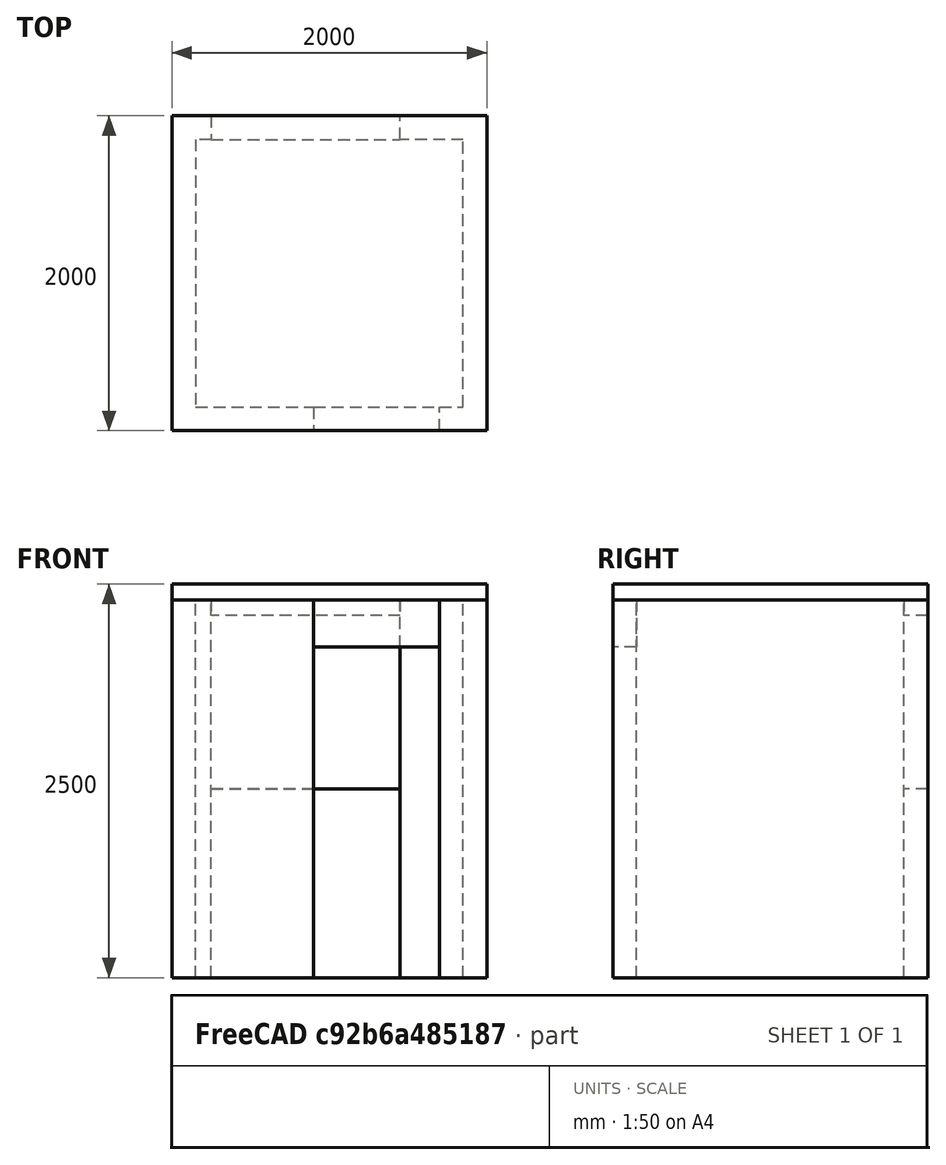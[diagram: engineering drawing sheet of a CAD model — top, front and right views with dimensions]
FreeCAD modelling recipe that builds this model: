
FCSTD DOCUMENT  (FreeCAD 0.16R6123 +2 (Git))
Label: cabin
License: CreativeCommons Attribution
LicenseURL: http://creativecommons.org/licenses/by/4.0/
objects: Part::Part2DObjectPython×22, App::FeaturePython×13, App::DocumentObjectGroup×6, Part::Extrusion×6, App::Annotation×3, Part::Feature×2
note: 30 computed .brp shape members not serialized (recipe doc carries the construction recipe); baked Part::Feature solids carry a one-line shape summary decoded from their .brp

FEATURE [Part::Part2DObjectPython] Rectangle  # Draft 2D object (typed FeaturePython)
  ChamferSize = 0
  Columns = 1
  FilletRadius = 0
  Height = 2000
  Length = 2000
  MakeFace = true
  Rows = 1
FEATURE [Part::Part2DObjectPython] Rectangle001  # Draft 2D object (typed FeaturePython)
  ChamferSize = 0
  Columns = 1
  FilletRadius = 0
  Height = 1700
  Length = 1700
  MakeFace = true
  Placement = pos=(150,150,0) rot=(0,0,1;0rad)
  Rows = 1
FEATURE [Part::Part2DObjectPython] Line  # Draft 2D object (typed FeaturePython)
  ChamferSize = 0
  Closed = false
  End = (1850,-930.924,0)
  FilletRadius = 0
  Length = 1930.92
  MakeFace = true
  Points = (2) [(1850,1000,0),(1850,-930.924,0)]
  Start = (1850,1000,0)
  Subdivisions = 0
FEATURE [Part::Part2DObjectPython] Line001  # Draft 2D object (typed FeaturePython)
  ChamferSize = 0
  Closed = false
  End = (1700,-930.924,0)
  FilletRadius = 0
  Length = 1930.92
  MakeFace = true
  Placement = pos=(-150,0,0) rot=(0,0,1;0rad)
  Points = (2) [(1850,1000,0),(1850,-930.924,0)]
  Start = (1700,1000,0)
  Subdivisions = 0
FEATURE [Part::Part2DObjectPython] Line002  # Draft 2D object (typed FeaturePython)
  ChamferSize = 0
  Closed = false
  End = (900,-930.924,0)
  FilletRadius = 0
  Length = 1930.92
  MakeFace = true
  Placement = pos=(-950,0,0) rot=(0,0,1;0rad)
  Points = (2) [(1850,1000,0),(1850,-930.924,0)]
  Start = (900,1000,0)
  Subdivisions = 0
FEATURE [Part::Part2DObjectPython] Line003  # Draft 2D object (typed FeaturePython)
  ChamferSize = 0
  Closed = false
  End = (150,2719.11,0)
  FilletRadius = 0
  Length = 1719.11
  MakeFace = true
  Points = (2) [(150,1000,0),(150,2719.11,0)]
  Start = (150,1000,0)
  Subdivisions = 0
FEATURE [Part::Part2DObjectPython] Line004  # Draft 2D object (typed FeaturePython)
  ChamferSize = 0
  Closed = false
  End = (250,2719.11,0)
  FilletRadius = 0
  Length = 1719.11
  MakeFace = true
  Placement = pos=(100,0,0) rot=(0,0,1;0rad)
  Points = (2) [(150,1000,0),(150,2719.11,0)]
  Start = (250,1000,0)
  Subdivisions = 0
FEATURE [Part::Part2DObjectPython] Line005  # Draft 2D object (typed FeaturePython)
  ChamferSize = 0
  Closed = false
  End = (1450,2719.11,0)
  FilletRadius = 0
  Length = 1719.11
  MakeFace = true
  Placement = pos=(1300,0,0) rot=(0,0,1;0rad)
  Points = (2) [(150,1000,0),(150,2719.11,0)]
  Start = (1450,1000,0)
  Subdivisions = 0
FEATURE [App::DocumentObjectGroup] Construction
  Group = -> [Rectangle,Rectangle001,Line,Line001,Line002,Line003,Line004,Line005]
FEATURE [Part::Part2DObjectPython] DWire  # Draft 2D object (typed FeaturePython)
  ChamferSize = 0
  Closed = true
  End = (0,0,0)
  FilletRadius = 0
  Length = 6000
  MakeFace = true
  Points = (8) [(0,2000,0),(250,2000,0),(250,1850,0),(150,1850,0),(150,150,0),(900,150,0),(900,0,0),(0,0,0)]
  Start = (0,2000,0)
  Subdivisions = 0
FEATURE [Part::Part2DObjectPython] DWire001  # Draft 2D object (typed FeaturePython)
  ChamferSize = 0
  Closed = true
  End = (1850,1850,0)
  FilletRadius = 0
  Length = 5400
  MakeFace = true
  Points = (8) [(1450,1850,0),(1450,2000,0),(2000,2000,0),(2000,0,0),(1700,0,0),(1700,150,0),(1850,150,0),(1850,1850,0)]
  Start = (1450,1850,0)
  Subdivisions = 0
FEATURE [Part::Part2DObjectPython] Line006  # Draft 2D object (typed FeaturePython)
  ChamferSize = 0
  Closed = false
  End = (1450,1925,0)
  FilletRadius = 0
  Length = 1200
  MakeFace = true
  Points = (2) [(250,1925,0),(1450,1925,0)]
  Start = (250,1925,0)
  Subdivisions = 0
FEATURE [Part::Part2DObjectPython] Line007  # Draft 2D object (typed FeaturePython)
  ChamferSize = 0
  Closed = false
  End = (1700,75,0)
  FilletRadius = 0
  Length = 800
  MakeFace = true
  Placement = pos=(1625,1775,0) rot=(0,0,-1;1.5708rad)
  Points = (2) [(900,75,0),(1700,75,0)]
  Start = (1700,875,0)
  Subdivisions = 0
FEATURE [Part::Part2DObjectPython] Arc  # Draft 2D object (typed FeaturePython)
  FirstAngle = 90
  LastAngle = 180
  MakeFace = true
  Placement = pos=(1700,75,0) rot=(0,0,1;0rad)
  Radius = 800
FEATURE [Part::Part2DObjectPython] Rectangle002  label="Tabletop"  # Draft 2D object (typed FeaturePython)
  ChamferSize = 0
  Columns = 1
  FilletRadius = 0
  Height = -600
  Length = 1700
  MakeFace = true
  Placement = pos=(150,1850,0) rot=(0,0,1;0rad)
  Rows = 1
FEATURE [Part::Feature] ENTITIES_  label="sink"
  Placement = pos=(-18300.5,-3837.71,0) rot=(0,0,1;0rad)
  shape: bbox 850 x 500 x 2e-07 mm, 0 faces, 0 solids (baked)
FEATURE [Part::Feature] ENTITIES_0  label="cooktop"
  Placement = pos=(-6228.71,-15812.2,-2.2e-11) rot=(0,0,1;0rad)
  shape: bbox 500 x 600 x 2e-07 mm, 0 faces, 0 solids (baked)
FEATURE [Part::Part2DObjectPython] Rectangle003  # Draft 2D object (typed FeaturePython)
  ChamferSize = 0
  Columns = 1
  FilletRadius = 0
  Height = -150
  Length = 1200
  MakeFace = true
  Placement = pos=(250,2000,0) rot=(0,0,1;0rad)
  Rows = 1
FEATURE [Part::Part2DObjectPython] Rectangle004  # Draft 2D object (typed FeaturePython)
  ChamferSize = 0
  Columns = 1
  FilletRadius = 0
  Height = 150
  Length = -800
  MakeFace = true
  Placement = pos=(1700,0,0) rot=(0,0,1;0rad)
  Rows = 1
FEATURE [App::FeaturePython] Dimension  # Draft dimension (typed FeaturePython)
  Dimline = (491.097,338.831,0)
  Direction = (0,0,0)
  Distance = 150
  End = (0,150,0)
  Normal = (0,0,1)
  Start = (0,0,0)
FEATURE [App::FeaturePython] Dimension003  # Draft dimension (typed FeaturePython)
  Dimline = (491.097,1850,0)
  Direction = (0,0,0)
  Distance = 150
  End = (250,2000,0)
  Normal = (0,0,1)
  Start = (250,1850,0)
FEATURE [App::FeaturePython] Dimension004  # Draft dimension (typed FeaturePython)
  Dimline = (491.097,1850,0)
  Direction = (0,0,0)
  Distance = 1700
  End = (150,1850,0)
  Normal = (0,0,1)
  Start = (150,150,0)
FEATURE [App::FeaturePython] Dimension005  # Draft dimension (typed FeaturePython)
  Dimline = (-280.313,430.313,0)
  Direction = (0,0,0)
  Distance = 150
  End = (150,0,0)
  Normal = (0,0,1)
  Start = (0,0,0)
FEATURE [App::FeaturePython] Dimension006  # Draft dimension (typed FeaturePython)
  Dimline = (0,430.313,0)
  Direction = (0,0,0)
  Distance = 1700
  End = (1850,150,0)
  Normal = (0,0,1)
  Start = (150,150,0)
FEATURE [App::FeaturePython] Dimension007  # Draft dimension (typed FeaturePython)
  Dimline = (1850,430.313,0)
  Direction = (0,0,0)
  Distance = 150
  End = (2000,150,0)
  Normal = (0,0,1)
  Start = (1850,150,0)
FEATURE [App::FeaturePython] Dimension008  # Draft dimension (typed FeaturePython)
  Dimline = (159.788,2397.37,0)
  Direction = (0,0,0)
  Distance = 250
  End = (250,2000,0)
  Normal = (0,0,1)
  Start = (0,2000,0)
FEATURE [App::FeaturePython] Dimension009  # Draft dimension (typed FeaturePython)
  Dimline = (171.744,2397.37,0)
  Direction = (0,0,0)
  Distance = 1200
  End = (1450,2000,0)
  Normal = (0,0,1)
  Start = (250,2000,0)
FEATURE [App::FeaturePython] Dimension010  # Draft dimension (typed FeaturePython)
  Dimline = (1268.19,2397.37,0)
  Direction = (0,0,0)
  Distance = 550
  End = (2000,2000,0)
  Normal = (0,0,1)
  Start = (1450,2000,0)
FEATURE [App::FeaturePython] Dimension011  # Draft dimension (typed FeaturePython)
  Dimline = (-372.676,1627.32,0)
  Direction = (0,0,0)
  Distance = 2000
  End = (0,2000,0)
  Normal = (0,0,1)
  Start = (0,0,0)
FEATURE [App::FeaturePython] Dimension012  # Draft dimension (typed FeaturePython)
  Dimline = (900,-572.516,0)
  Direction = (0,0,0)
  Distance = 900
  End = (900,0,0)
  Normal = (0,0,1)
  Start = (0,0,0)
FEATURE [App::FeaturePython] Dimension013  # Draft dimension (typed FeaturePython)
  Dimline = (900,-572.516,0)
  Direction = (0,0,0)
  Distance = 800
  End = (1700,0,0)
  Normal = (0,0,1)
  Start = (900,0,0)
FEATURE [App::FeaturePython] Dimension014  # Draft dimension (typed FeaturePython)
  Dimline = (1700,-572.516,0)
  Direction = (0,0,0)
  Distance = 300
  End = (2000,0,0)
  Normal = (0,0,1)
  Start = (1700,0,0)
FEATURE [Part::Part2DObjectPython] DWire002  # Draft 2D object (typed FeaturePython)
  ChamferSize = 0
  Closed = false
  End = (1363.02,83.2838,0)
  FilletRadius = 0
  Length = 1405.75
  MakeFace = true
  Points = (3) [(2622.62,-269.561,0),(1715.86,-269.561,0),(1363.02,83.2838,0)]
  Start = (2622.62,-269.561,0)
  Subdivisions = 0
FEATURE [App::Annotation] Text
  LabelText = wooden door
  Position = (2665.06,-304.996,0)
FEATURE [Part::Part2DObjectPython] Line008  # Draft 2D object (typed FeaturePython)
  ChamferSize = 0
  Closed = false
  End = (1776,1520.9,0)
  FilletRadius = 0
  Length = 906.803
  MakeFace = true
  Points = (2) [(2682.8,1520.9,0),(1776,1520.9,0)]
  Start = (2682.8,1520.9,0)
  Subdivisions = 0
FEATURE [App::Annotation] Text001
  LabelText = wooden tabletop | height = 1.10m
  Position = (2760.04,1562.41,0)
FEATURE [Part::Part2DObjectPython] DWire003  # Draft 2D object (typed FeaturePython)
  ChamferSize = 0
  Closed = false
  End = (967.987,1949.52,0)
  FilletRadius = 0
  Length = 1831.67
  MakeFace = true
  Points = (3) [(2696.08,2244.4,0),(1335.95,2244.4,0),(967.987,1949.52,0)]
  Start = (2696.08,2244.4,0)
  Subdivisions = 0
FEATURE [App::Annotation] Text002
  LabelText = aluminium window frame | with single-thickness glass
  Position = (2764.09,2281.21,0)
FEATURE [App::DocumentObjectGroup] Group  label="Annotations"
  Group = -> [Dimension,Dimension003,Dimension004,Dimension005,Dimension006,Dimension007,Dimension008,Dimension009,Dimension010,Dimension011,Dimension012,Dimension013,Dimension014,DWire002,Text,Line008,Text001,DWire003,Text002]
FEATURE [App::DocumentObjectGroup] Group001  label="Furniture"
  Group = -> [ENTITIES_0,ENTITIES_,Rectangle002]
FEATURE [App::DocumentObjectGroup] Group002  label="Doors & Windows"
  Group = -> [Line006,Rectangle003,Arc,Line007,Rectangle004]
FEATURE [Part::Extrusion] Extrusion
  Base = -> DWire
  Dir = (0,0,2400)
  Solid = true
FEATURE [Part::Extrusion] Extrusion001
  Base = -> DWire001
  Dir = (0,0,2400)
  Solid = true
FEATURE [Part::Part2DObjectPython] Rectangle005  # Draft 2D object (typed FeaturePython)
  ChamferSize = 0
  Columns = 1
  FilletRadius = 0
  Height = -150
  Length = 800
  MakeFace = true
  Placement = pos=(900,150,2400) rot=(0,0,1;0rad)
  Rows = 1
  Support = -> Extrusion
FEATURE [Part::Extrusion] Extrusion002
  Base = -> Rectangle005
  Dir = (0,0,-300)
  Solid = true
FEATURE [Part::Part2DObjectPython] Rectangle006  # Draft 2D object (typed FeaturePython)
  ChamferSize = 0
  Columns = 1
  FilletRadius = 0
  Height = -150
  Length = -1200
  MakeFace = true
  Placement = pos=(1450,2000,2400) rot=(0,0,1;0rad)
  Rows = 1
FEATURE [Part::Extrusion] Extrusion003
  Base = -> Rectangle003
  Dir = (0,0,1200)
  Solid = true
FEATURE [Part::Extrusion] Extrusion004
  Base = -> Rectangle006
  Dir = (0,0,-100)
  Solid = true
FEATURE [Part::Part2DObjectPython] Rectangle007  # Draft 2D object (typed FeaturePython)
  ChamferSize = 0
  Columns = 1
  FilletRadius = 0
  Height = 2000
  Length = 2000
  MakeFace = true
  Placement = pos=(0,0,2400) rot=(0,0,1;0rad)
  Rows = 1
FEATURE [Part::Extrusion] Extrusion005
  Base = -> Rectangle007
  Dir = (0,0,100)
  Solid = true
FEATURE [App::DocumentObjectGroup] Group003  label="Walls"
  Group = -> [DWire,DWire001,Extrusion,Extrusion001,Extrusion002,Extrusion003,Extrusion004,Extrusion005]
FEATURE [App::DocumentObjectGroup] Group004  label="Floor plan"
  Group = -> [Construction,Group001,Group002,Group003,Group]
